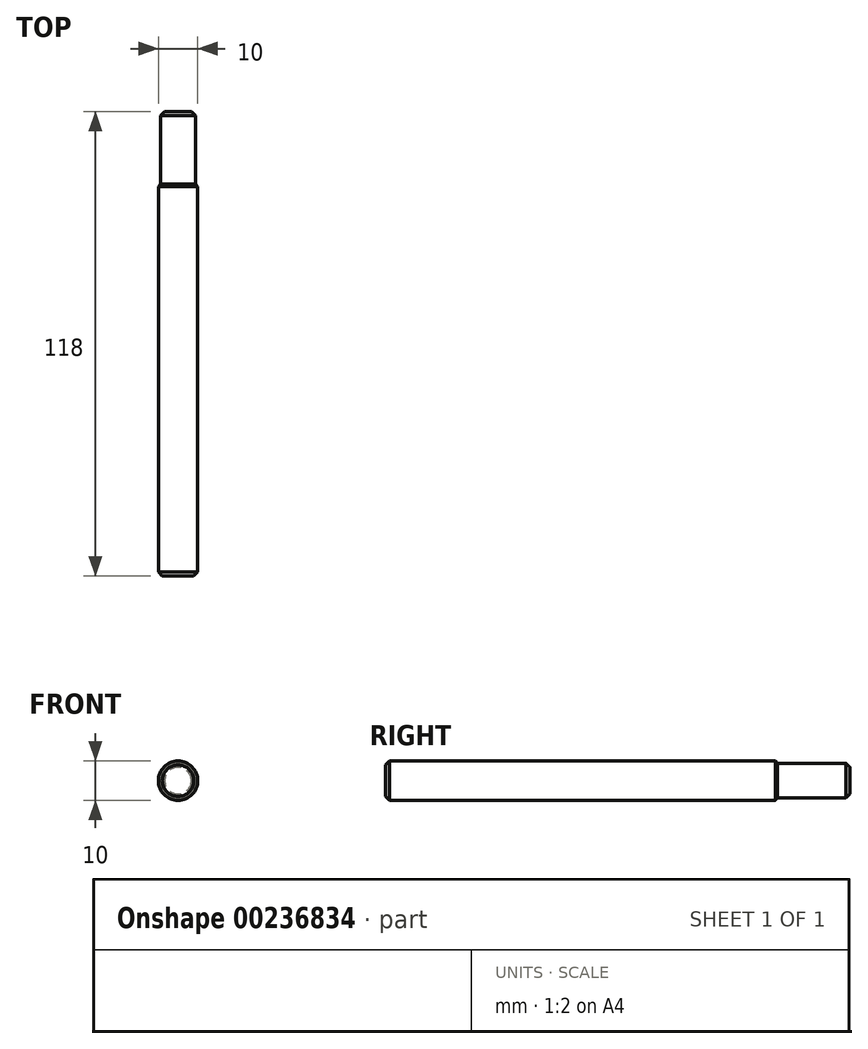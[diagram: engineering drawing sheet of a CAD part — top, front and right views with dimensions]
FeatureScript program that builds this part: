
annotation { "Feature Type Name" : "Feature", "Feature Type Description" : "" }
export const myFeature = defineFeature(function(context is Context, id is Id, definition is map)
    precondition{}
    {
        {
            var Q0;
            Q0=qCreatedBy(makeId("Front.planeOp"),FACE);
            var sketch = newSketch(context, id + "F0", { "sketchPlane" : qUnion([Q0])});
            skCircle(sketch, "E0", {"center": v(0, 0) * mm, "radius": 5 * mm});
            skSolve(sketch);
        }
        {
            var Q0;
            Q0 = qSketchRegion(id + "F0", true);
            extrude(context, id + "F1", {"entities" : qUnion([Q0]), "depth" : 100 * mm});
        }
        {
            var Q0;
            Q0=makeQuery(id+"F1.opExtrude","CAP_FACE",FACE,{"disambiguationData":[OSD([sQuery(id+"F0.wireOp",EDGE,"E0")])],"isStart":true});
            var sketch = newSketch(context, id + "F2", { "sketchPlane" : qUnion([Q0])});
            skCircle(sketch, "E1", {"center": v(0, 0) * mm, "radius": 4.4 * mm});
            skSolve(sketch);
        }
        {
            var Q0;
            Q0 = qSketchRegion(id + "F2", true);
            extrude(context, id + "F3", {"entities" : qUnion([Q0]), "operationType" : NewBodyOperationType.ADD, "depth" : 18 * mm});
        }
        {
            var Q0;
            Q0=makeQuery(id+"F1.opExtrude","CAP_EDGE",EDGE,{"disambiguationData":[OSD([sQuery(id+"F0.wireOp",EDGE,"E0")])],"isStart":true});
            chamfer(context, id + "F4", {"entities" : qUnion([Q0]), "width" : 1 * mm, "tangentPropagation" : true});
        }
        {
            var Q0;
            Q0=makeQuery(id+"F1.opExtrude","CAP_EDGE",EDGE,{"disambiguationData":[OSD([sQuery(id+"F0.wireOp",EDGE,"E0")])],"isStart":false});
            var Q1;
            Q1=makeQuery(id+"F3.opExtrude","CAP_EDGE",EDGE,{"disambiguationData":[OSD([sQuery(id+"F2.wireOp",EDGE,"E1")])],"isStart":false});
            chamfer(context, id + "F5", {"entities" : qUnion([Q0, Q1]), "width" : 1 * mm, "tangentPropagation" : true});
        }
    });
